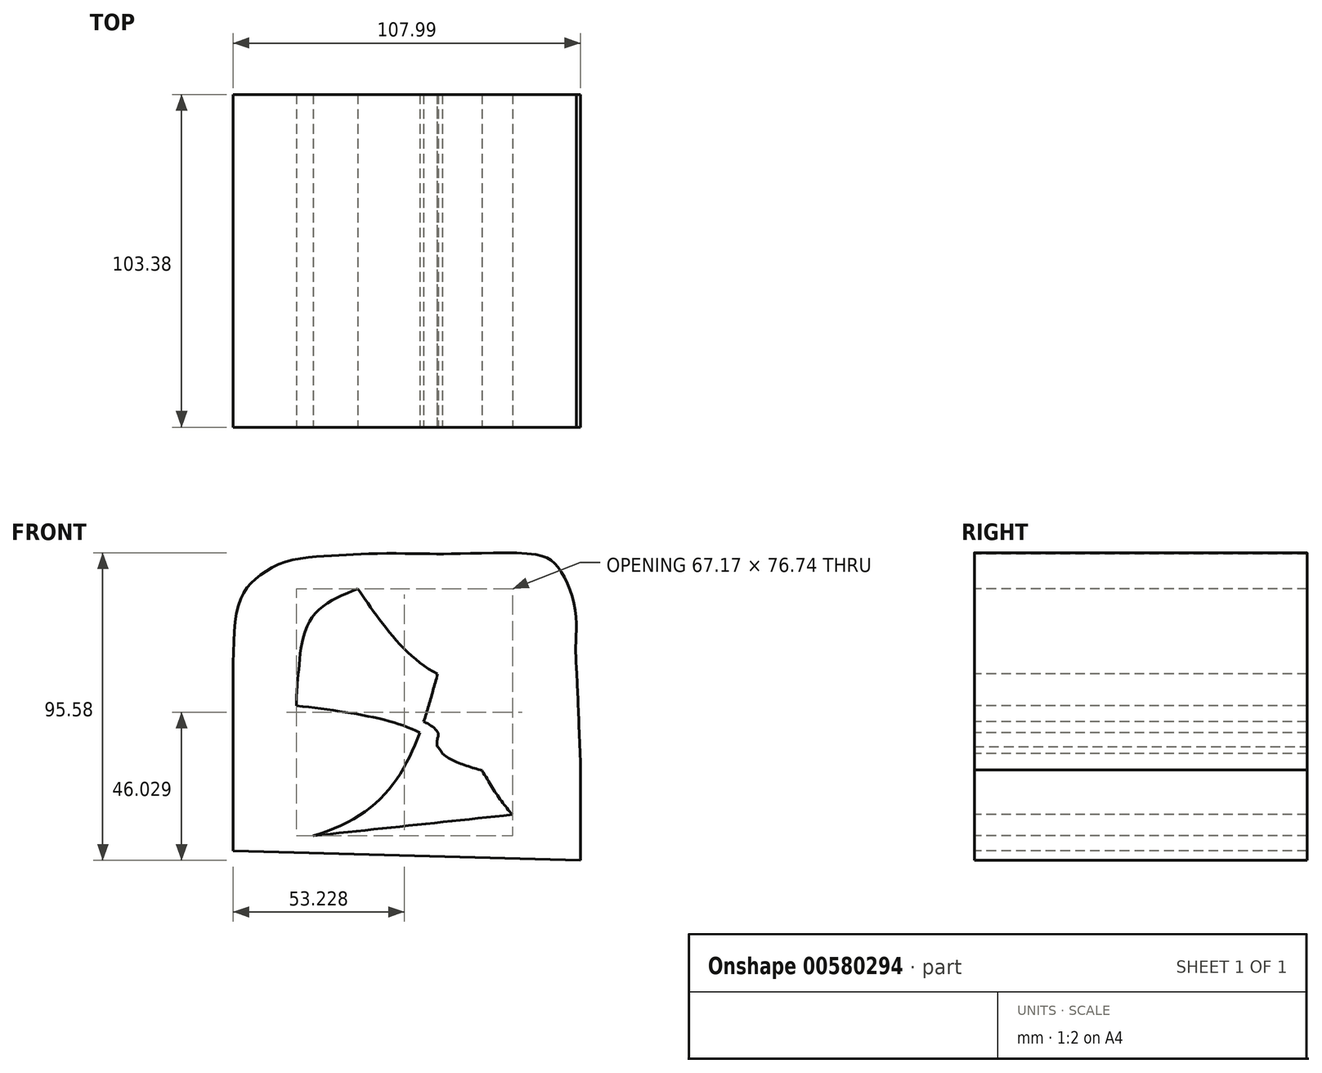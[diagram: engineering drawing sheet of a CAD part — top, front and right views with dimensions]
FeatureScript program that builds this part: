
annotation { "Feature Type Name" : "Feature", "Feature Type Description" : "" }
export const myFeature = defineFeature(function(context is Context, id is Id, definition is map)
    precondition{}
    {
        {
            var Q0;
            Q0=qCreatedBy(makeId("Front.planeOp"),FACE);
            var sketch = newSketch(context, id + "F0", { "sketchPlane" : qUnion([Q0])});
            skFitSpline(sketch, "E0", {"points": [v(-63.52, 0) * mm, v(-61.7, 21.93) * mm, v(-56.57, 29.5) * mm, v(-46.89, 34.94) * mm, v(-32.97, 36.75) * mm, v(-21.48, 37.36) * mm, v(-5.14, 37.36) * mm, v(6.65, 37.36) * mm, v(30.55, 37.06) * mm, v(37.5, 33.12) * mm, v(42.65, 20.72) * mm, v(42.95, 8.92) * mm, v(43.26, 0) * mm, v(44.47, -29.8) * mm], "startDerivative": vector(2.19, 260.41) * mm, "endDerivative": vector(11.5, -309.17) * mm});
            skFitSpline(sketch, "E1", {"points": [v(-63.52, 0) * mm, v(-63.52, -39.78) * mm, v(-63.52, -54.9) * mm], "startDerivative": vector(0, -71.93) * mm, "endDerivative": vector(0, -34.95) * mm});
            skFitSpline(sketch, "E2", {"points": [v(44.47, -29.8) * mm, v(44.47, -57.93) * mm], "startDerivative": vector(0, -28.13) * mm, "endDerivative": vector(0, -28.13) * mm});
            skFitSpline(sketch, "E3", {"points": [v(43.26, 0) * mm, v(0, 0) * mm, v(-24.8, 26.47) * mm, v(-32.97, 36.75) * mm], "startDerivative": vector(-115.3, -22.33) * mm, "endDerivative": vector(-32.36, 37.46) * mm});
            skFitSpline(sketch, "E4", {"points": [v(-63.52, 0) * mm, v(0, 0) * mm, v(30.55, 37.06) * mm], "startDerivative": vector(132.95, -21.3) * mm, "endDerivative": vector(53.35, 98.2) * mm});
            skFitSpline(sketch, "E5", {"points": [v(0, 0) * mm, v(-26.32, -45.22) * mm, v(-63.52, -54.9) * mm, v(-63.45, -54.9) * mm], "startDerivative": vector(-27.58, -101.99) * mm, "endDerivative": vector(5.77, 0.15) * mm});
            skFitSpline(sketch, "E6", {"points": [v(0, 0) * mm, v(23.3, -43.71) * mm, v(44.47, -57.93) * mm], "startDerivative": vector(36.9, -87.03) * mm, "endDerivative": vector(52.91, -25.45) * mm});
            skFitSpline(sketch, "E7", {"points": [v(-63.45, -54.9) * mm, v(44.47, -57.93) * mm], "startDerivative": vector(107.92, -3.02) * mm, "endDerivative": vector(107.92, -3.02) * mm});
            skFitSpline(sketch, "E8", {"points": [v(0, 0) * mm, v(0, 21.93) * mm, v(13.86, 10.86) * mm], "startDerivative": vector(-7.7, 58.74) * mm, "endDerivative": vector(36.13, -38.7) * mm});
            skFitSpline(sketch, "E9", {"points": [v(13.86, 10.86) * mm, v(23.92, -3.13) * mm, v(27.22, -20.42) * mm, v(21.17, -29.8) * mm, v(13.86, -29.95) * mm, v(3.02, -25.86) * mm, v(0, -22.54) * mm, v(0, -20.12) * mm, v(0, -17.95) * mm, v(-4.32, -14.83) * mm, v(-4.85, -14.83) * mm], "startDerivative": vector(69.5, -80.77) * mm, "endDerivative": vector(-12.93, -4.71) * mm});
            skFitSpline(sketch, "E10", {"points": [v(-24.8, 26.47) * mm, v(-39.32, 17.1) * mm, v(-43.26, 0) * mm, v(-43.86, -9.83) * mm, v(-43.26, -16.79) * mm, v(-43.26, -18.6) * mm, v(-43.26, -22.84) * mm, v(-42.35, -27.38) * mm, v(-42.05, -31.3) * mm, v(-39.93, -44.01) * mm], "startDerivative": vector(-104.36, -42.57) * mm, "endDerivative": vector(19.47, -102.84) * mm});
            skFitSpline(sketch, "E11", {"points": [v(-38.69, -50.27) * mm, v(23.3, -43.71) * mm], "startDerivative": vector(61.99, 6.53) * mm, "endDerivative": vector(61.99, 6.53) * mm});
            skFitSpline(sketch, "E12", {"points": [v(2.63, -45.89) * mm, v(0, -22.54) * mm, v(-43.86, -9.83) * mm], "startDerivative": vector(8.12, 63.02) * mm, "endDerivative": vector(-95.42, 11.9) * mm});
            skSolve(sketch);
        }
        {
            var Q0;
            {var subQ0=sQuery(id+"F0.wireOp",EDGE,"E1");Q0=makeQuery(id+"F0.imprint","IMPRINT",FACE,{"disambiguationData":[TD([[makeQuery(id+"F0.imprint","IMPRINT",EDGE,{"derivedFrom":subQ0}),1.0]])]});}
            var Q1;
            {var subQ1=sQuery(id+"F0.wireOp",EDGE,"E0");var subQ3=sQuery(id+"F0.wireOp",EDGE,"E3");var subQ4=makeQuery(id+"F0.imprint","INTERSECT",VERTEX,{"disambiguationData":[OD(1.0)],"derivedFrom":[subQ1,subQ3]});Q1=makeQuery(id+"F0.imprint","IMPRINT",FACE,{"disambiguationData":[TD([[makeQuery(id+"F0.imprint","IMPRINT",EDGE,{"disambiguationData":[TD([[subQ4,1.0]])],"derivedFrom":subQ1}),-1.0]])]});}
            var Q2;
            {var subQ5=sQuery(id+"F0.wireOp",EDGE,"E8");Q2=makeQuery(id+"F0.imprint","IMPRINT",FACE,{"disambiguationData":[TD([[makeQuery(id+"F0.imprint","IMPRINT",EDGE,{"derivedFrom":subQ5}),1.0]])]});}
            var Q3;
            {var subQ0=sQuery(id+"F0.wireOp",EDGE,"E8");Q3=makeQuery(id+"F0.imprint","IMPRINT",FACE,{"disambiguationData":[TD([[makeQuery(id+"F0.imprint","IMPRINT",EDGE,{"derivedFrom":subQ0}),-1.0]])]});}
            var Q4;
            {var subQ2=sQuery(id+"F0.wireOp",EDGE,"E3");var subQ4=sQuery(id+"F0.wireOp",EDGE,"E9");var subQ5=makeQuery(id+"F0.imprint","INTERSECT",VERTEX,{"derivedFrom":[subQ2,subQ4]});Q4=makeQuery(id+"F0.imprint","IMPRINT",FACE,{"disambiguationData":[TD([[makeQuery(id+"F0.imprint","IMPRINT",EDGE,{"disambiguationData":[TD([[subQ5,1.0]])],"derivedFrom":subQ4}),-1.0]])]});}
            var Q5;
            {var subQ1=sQuery(id+"F0.wireOp",EDGE,"E3");var subQ3=sQuery(id+"F0.wireOp",EDGE,"E9");var subQ4=makeQuery(id+"F0.imprint","INTERSECT",VERTEX,{"derivedFrom":[subQ1,subQ3]});Q5=makeQuery(id+"F0.imprint","IMPRINT",FACE,{"disambiguationData":[TD([[makeQuery(id+"F0.imprint","IMPRINT",EDGE,{"disambiguationData":[TD([[subQ4,-1.0]])],"derivedFrom":subQ3}),-1.0]])]});}
            var Q6;
            {var subQ1=sQuery(id+"F0.wireOp",EDGE,"E5");var subQ3=sQuery(id+"F0.wireOp",EDGE,"E9");var subQ4=makeQuery(id+"F0.imprint","INTERSECT",VERTEX,{"derivedFrom":[subQ1,subQ3]});Q6=makeQuery(id+"F0.imprint","IMPRINT",FACE,{"disambiguationData":[TD([[makeQuery(id+"F0.imprint","IMPRINT",EDGE,{"disambiguationData":[TD([[subQ4,1.0]])],"derivedFrom":subQ3}),-1.0]])]});}
            var Q7;
            {var subQ1=sQuery(id+"F0.wireOp",EDGE,"E2");Q7=makeQuery(id+"F0.imprint","IMPRINT",FACE,{"disambiguationData":[TD([[makeQuery(id+"F0.imprint","IMPRINT",EDGE,{"derivedFrom":subQ1}),-1.0]])]});}
            var Q8;
            {var subQ0=sQuery(id+"F0.wireOp",EDGE,"E3");var subQ1=sQuery(id+"F0.wireOp",EDGE,"E0");var subQ2=makeQuery(id+"F0.imprint","INTERSECT",VERTEX,{"disambiguationData":[OD(0.0)],"derivedFrom":[subQ1,subQ0]});Q8=makeQuery(id+"F0.imprint","IMPRINT",FACE,{"disambiguationData":[TD([[makeQuery(id+"F0.imprint","IMPRINT",EDGE,{"disambiguationData":[TD([[subQ2,1.0]])],"derivedFrom":subQ1}),-1.0]])]});}
            var Q9;
            {var subQ0=sQuery(id+"F0.wireOp",EDGE,"E7");Q9=makeQuery(id+"F0.imprint","IMPRINT",FACE,{"disambiguationData":[TD([[makeQuery(id+"F0.imprint","IMPRINT",EDGE,{"derivedFrom":subQ0}),1.0]])]});}
            extrude(context, id + "F1", {"entities" : qUnion([Q0, Q1, Q2, Q3, Q4, Q5, Q6, Q7, Q8, Q9]), "oppositeDirection" : true, "depth" : 65.8 * mm, "offsetDistance" : 25.4 * mm});
        }
        {
            var Q0;
            {var subQ1=sQuery(id+"F0.wireOp",EDGE,"E0");var subQ3=sQuery(id+"F0.wireOp",EDGE,"E3");var subQ4=makeQuery(id+"F0.imprint","INTERSECT",VERTEX,{"disambiguationData":[OD(1.0)],"derivedFrom":[subQ1,subQ3]});Q0=makeQuery(id+"F0.imprint","IMPRINT",FACE,{"disambiguationData":[TD([[makeQuery(id+"F0.imprint","IMPRINT",EDGE,{"disambiguationData":[TD([[subQ4,1.0]])],"derivedFrom":subQ3}),1.0]])]});}
            var Q1;
            {var subQ0=sQuery(id+"F0.wireOp",EDGE,"E3");var subQ1=sQuery(id+"F0.wireOp",EDGE,"E0");var subQ2=makeQuery(id+"F0.imprint","INTERSECT",VERTEX,{"disambiguationData":[OD(0.0)],"derivedFrom":[subQ1,subQ0]});Q1=makeQuery(id+"F0.imprint","IMPRINT",FACE,{"disambiguationData":[TD([[makeQuery(id+"F0.imprint","IMPRINT",EDGE,{"disambiguationData":[TD([[subQ2,1.0]])],"derivedFrom":subQ1}),-1.0]])]});}
            var Q2;
            {var subQ0=sQuery(id+"F0.wireOp",EDGE,"E7");Q2=makeQuery(id+"F0.imprint","IMPRINT",FACE,{"disambiguationData":[TD([[makeQuery(id+"F0.imprint","IMPRINT",EDGE,{"derivedFrom":subQ0}),1.0]])]});}
            var Q3;
            {var subQ6=sQuery(id+"F0.wireOp",EDGE,"E8");Q3=makeQuery(id+"F0.imprint","IMPRINT",FACE,{"disambiguationData":[TD([[makeQuery(id+"F0.imprint","IMPRINT",EDGE,{"derivedFrom":subQ6}),1.0]])]});}
            var Q4;
            {var subQ8=sQuery(id+"F0.wireOp",EDGE,"E2");Q4=makeQuery(id+"F0.imprint","IMPRINT",FACE,{"disambiguationData":[TD([[makeQuery(id+"F0.imprint","IMPRINT",EDGE,{"derivedFrom":subQ8}),-1.0]])]});}
            var Q5;
            {var subQ1=sQuery(id+"F0.wireOp",EDGE,"E1");Q5=makeQuery(id+"F0.imprint","IMPRINT",FACE,{"disambiguationData":[TD([[makeQuery(id+"F0.imprint","IMPRINT",EDGE,{"derivedFrom":subQ1}),1.0]])]});}
            var Q6;
            Q6=makeQuery(id+"F1.opExtrude","CAP_FACE",FACE,{"disambiguationData":[OSD([sQuery(id+"F0.wireOp",EDGE,"E0"),sQuery(id+"F0.wireOp",EDGE,"E1"),sQuery(id+"F0.wireOp",EDGE,"E2"),sQuery(id+"F0.wireOp",EDGE,"E3"),sQuery(id+"F0.wireOp",EDGE,"E5"),sQuery(id+"F0.wireOp",EDGE,"E6"),sQuery(id+"F0.wireOp",EDGE,"E7"),sQuery(id+"F0.wireOp",EDGE,"E9"),sQuery(id+"F0.wireOp",EDGE,"E10"),sQuery(id+"F0.wireOp",EDGE,"E11"),sQuery(id+"F0.wireOp",EDGE,"E12")])],"isStart":true});
            var Q7;
            Q7=makeQuery(id+"F1.opExtrude","CAP_FACE",FACE,{"disambiguationData":[OSD([sQuery(id+"F0.wireOp",EDGE,"E0"),sQuery(id+"F0.wireOp",EDGE,"E1"),sQuery(id+"F0.wireOp",EDGE,"E2"),sQuery(id+"F0.wireOp",EDGE,"E3"),sQuery(id+"F0.wireOp",EDGE,"E5"),sQuery(id+"F0.wireOp",EDGE,"E6"),sQuery(id+"F0.wireOp",EDGE,"E7"),sQuery(id+"F0.wireOp",EDGE,"E9"),sQuery(id+"F0.wireOp",EDGE,"E10"),sQuery(id+"F0.wireOp",EDGE,"E11"),sQuery(id+"F0.wireOp",EDGE,"E12")])],"isStart":false});
            extrude(context, id + "F2", {"entities" : qUnion([Q0, Q1, Q2, Q3, Q4, Q5, Q6, Q7]), "operationType" : NewBodyOperationType.ADD, "depth" : 37.6 * mm, "offsetDistance" : 25.4 * mm});
        }
    });
